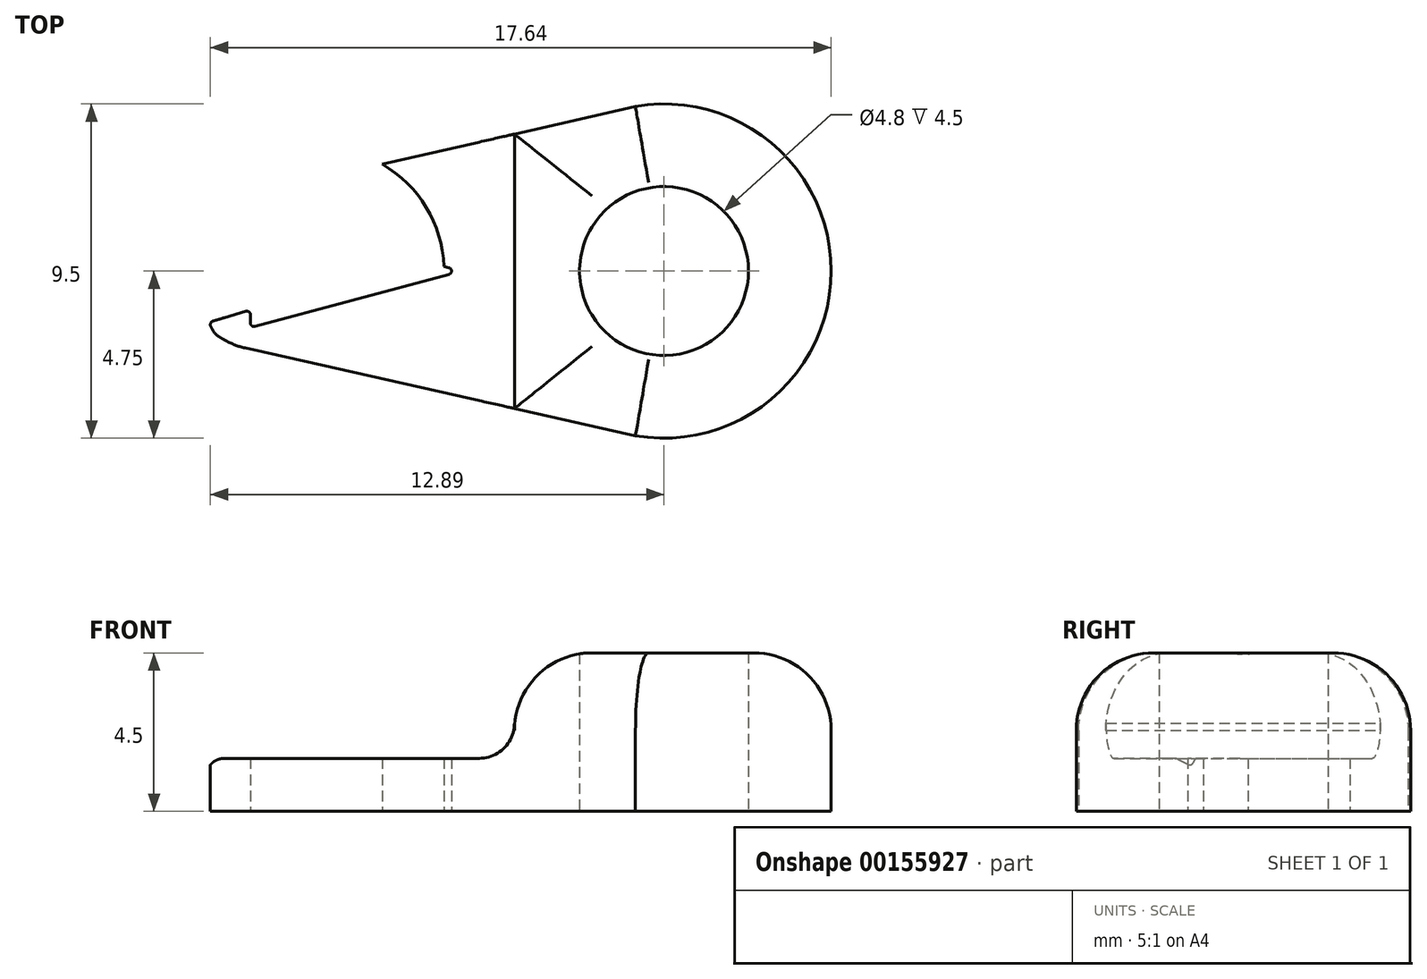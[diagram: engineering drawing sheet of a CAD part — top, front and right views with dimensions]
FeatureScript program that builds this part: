
annotation { "Feature Type Name" : "Feature", "Feature Type Description" : "" }
export const myFeature = defineFeature(function(context is Context, id is Id, definition is map)
    precondition{}
    {
        {
            var Q0;
            Q0=qCreatedBy(makeId("Top.planeOp"),FACE);
            var sketch = newSketch(context, id + "F0", { "sketchPlane" : qUnion([Q0])});
            skCircle(sketch, "E0", {"center": v(0, 0) * mm, "radius": 4.75 * mm});
            skCircle(sketch, "E1", {"center": v(0, 0) * mm, "radius": 2.4 * mm});
            skLineSegment(sketch, "E2", {"start": v(0, 0) * mm, "end": v(-5.75, 0) * mm});
            skArc(sketch, "E3", {"start": v(-12.88, -1.56) * mm, "mid": v(-12.85, -1.62) * mm, "end": v(-12.82, -1.68) * mm});
            skLineSegment(sketch, "E4", {"start": v(-6.11, 0.1) * mm, "end": v(-11.62, 1.57) * mm});
            skLineSegment(sketch, "E5", {"start": v(-6.11, -0.1) * mm, "end": v(-11.62, -1.57) * mm});
            skLineSegment(sketch, "E6", {"start": v(-11.75, 1.6) * mm, "end": v(-11.75, 1.1) * mm});
            skLineSegment(sketch, "E7", {"start": v(-11.75, 1.47) * mm, "end": v(-11.75, 1.23) * mm});
            skLineSegment(sketch, "E8", {"start": v(-11.87, 1.14) * mm, "end": v(-12.84, 1.37) * mm});
            skLineSegment(sketch, "E9", {"start": v(-11.75, -1.6) * mm, "end": v(-11.75, -1.1) * mm});
            skLineSegment(sketch, "E10", {"start": v(-11.88, -1.15) * mm, "end": v(-12.82, -1.42) * mm});
            skLineSegment(sketch, "E11.trimOffspring", {"start": v(-11.75, -1.24) * mm, "end": v(-11.75, -1.48) * mm});
            skArc(sketch, "E12.trimOffspring", {"start": v(-6.25, 0.13) * mm, "mid": v(-6.75, 1.81) * mm, "end": v(-8, 3.03) * mm});
            skPoint(sketch, "E13.endSnap0", {"position": v(-11.34, -2.73) * mm});
            skPoint(sketch, "E13.end.orphan", {"position": v(-12.93, -2.73) * mm});
            skLineSegment(sketch, "E14", {"start": v(-12.66, 1.82) * mm, "end": v(-12.5, 1.91) * mm});
            skLineSegment(sketch, "E15", {"start": v(-11.9, -2.19) * mm, "end": v(-0.8, -4.68) * mm});
            skLineSegment(sketch, "E16", {"start": v(-12.63, -1.88) * mm, "end": v(-12.45, -1.98) * mm});
            skArc(sketch, "E17.trimOffspring", {"start": v(-12.85, 1.62) * mm, "mid": v(-12.88, 1.57) * mm, "end": v(-12.9, 1.51) * mm});
            skLineSegment(sketch, "E18.trimOffspring", {"start": v(-0.94, 4.66) * mm, "end": v(-0.81, 4.68) * mm});
            skLineSegment(sketch, "E19.trimOffspring", {"start": v(-11.95, 2.13) * mm, "end": v(-0.81, 4.68) * mm});
            skPoint(sketch, "E20.orphan", {"position": v(-12.96, 1.9) * mm});
            skArc(sketch, "E21.trimOffspring", {"start": v(-8.04, -3.05) * mm, "mid": v(-6.77, -1.83) * mm, "end": v(-6.25, -0.13) * mm});
            skPoint(sketch, "E22.orphan", {"position": v(-9.75, -3.5) * mm});
            skPoint(sketch, "E23.orphan", {"position": v(-12.93, -1.96) * mm});
            skPoint(sketch, "E24.end.orphan", {"position": v(-12.93, -1.7) * mm});
            skPoint(sketch, "E25.end.orphan", {"position": v(-12.96, 1.65) * mm});
            skPoint(sketch, "E26.visualSharp", {"position": v(-11.75, 1.6) * mm});
            skArc(sketch, "E26.filletArc", {"start": v(-11.62, 1.57) * mm, "mid": v(-11.7, 1.55) * mm, "end": v(-11.75, 1.47) * mm});
            skPoint(sketch, "E27.visualSharp", {"position": v(-5.75, 0) * mm});
            skArc(sketch, "E27.filletArc", {"start": v(-6.11, -0.1) * mm, "mid": v(-6.04, 0) * mm, "end": v(-6.11, 0.1) * mm});
            skPoint(sketch, "E28.visualSharp", {"position": v(-11.75, -1.6) * mm});
            skArc(sketch, "E28.filletArc", {"start": v(-11.75, -1.48) * mm, "mid": v(-11.71, -1.56) * mm, "end": v(-11.62, -1.57) * mm});
            skPoint(sketch, "E29.visualSharp", {"position": v(-11.75, -1.1) * mm});
            skArc(sketch, "E29.filletArc", {"start": v(-11.75, -1.24) * mm, "mid": v(-11.8, -1.16) * mm, "end": v(-11.88, -1.15) * mm});
            skPoint(sketch, "E30.visualSharp", {"position": v(-11.75, 1.1) * mm});
            skArc(sketch, "E30.filletArc", {"start": v(-11.87, 1.14) * mm, "mid": v(-11.79, 1.16) * mm, "end": v(-11.75, 1.23) * mm});
            skPoint(sketch, "E31.visualSharp", {"position": v(-12.93, -1.46) * mm});
            skArc(sketch, "E31.filletArc", {"start": v(-12.82, -1.42) * mm, "mid": v(-12.88, -1.48) * mm, "end": v(-12.88, -1.56) * mm});
            skPoint(sketch, "E32.visualSharp", {"position": v(-12.96, 1.4) * mm});
            skArc(sketch, "E32.filletArc", {"start": v(-12.9, 1.51) * mm, "mid": v(-12.9, 1.43) * mm, "end": v(-12.84, 1.37) * mm});
            skPoint(sketch, "E33.visualSharp", {"position": v(-12.78, 1.75) * mm});
            skArc(sketch, "E33.filletArc", {"start": v(-12.66, 1.82) * mm, "mid": v(-12.77, 1.74) * mm, "end": v(-12.85, 1.62) * mm});
            skPoint(sketch, "E34.visualSharp", {"position": v(-12.24, 2.06) * mm});
            skArc(sketch, "E34.filletArc", {"start": v(-11.95, 2.13) * mm, "mid": v(-12.23, 2.04) * mm, "end": v(-12.5, 1.91) * mm});
            skPoint(sketch, "E35.visualSharp", {"position": v(-12.2, -2.12) * mm});
            skArc(sketch, "E35.filletArc", {"start": v(-12.45, -1.98) * mm, "mid": v(-12.19, -2.1) * mm, "end": v(-11.9, -2.19) * mm});
            skPoint(sketch, "E36.visualSharp", {"position": v(-12.74, -1.81) * mm});
            skArc(sketch, "E36.filletArc", {"start": v(-12.82, -1.68) * mm, "mid": v(-12.74, -1.8) * mm, "end": v(-12.63, -1.88) * mm});
            skLineSegment(sketch, "E37", {"start": v(-12.96, 1.8) * mm, "end": v(-12.93, -2.85) * mm});
            skSolve(sketch);
        }
        {
            var Q0;
            Q0=qCreatedBy(makeId("Front.planeOp"),FACE);
            var sketch = newSketch(context, id + "F1", { "sketchPlane" : qUnion([Q0])});
            skLineSegment(sketch, "E38", {"start": v(0, 0) * mm, "end": v(-13, 0) * mm});
            skLineSegment(sketch, "E39", {"start": v(-13, 0) * mm, "end": v(-13, 1) * mm});
            skLineSegment(sketch, "E40", {"start": v(-12.5, 1.5) * mm, "end": v(-8, 1.5) * mm});
            skLineSegment(sketch, "E41", {"start": v(-8, 1.5) * mm, "end": v(-5.25, 1.5) * mm});
            skLineSegment(sketch, "E42", {"start": v(-4.25, 2.3) * mm, "end": v(-4.25, 2.5) * mm});
            skLineSegment(sketch, "E43", {"start": v(-2.05, 4.5) * mm, "end": v(0, 4.5) * mm});
            skLineSegment(sketch, "E44", {"start": v(0, 4.5) * mm, "end": v(0, 0) * mm});
            skPoint(sketch, "E45.visualSharp", {"position": v(-4.25, 4.5) * mm});
            skArc(sketch, "E45.filletArc", {"start": v(-2.05, 4.5) * mm, "mid": v(-3.6, 3.86) * mm, "end": v(-4.25, 2.3) * mm});
            skPoint(sketch, "E46.visualSharp", {"position": v(-13, 1.5) * mm});
            skArc(sketch, "E46.filletArc", {"start": v(-12.5, 1.5) * mm, "mid": v(-12.85, 1.35) * mm, "end": v(-13, 1) * mm});
            skPoint(sketch, "E47.visualSharp", {"position": v(-4.25, 1.5) * mm});
            skArc(sketch, "E47.filletArc", {"start": v(-5.25, 1.5) * mm, "mid": v(-4.54, 1.8) * mm, "end": v(-4.25, 2.5) * mm});
            skLineSegment(sketch, "E48", {"start": v(0, 4.5) * mm, "end": v(0, 5.81) * mm});
            skLineSegment(sketch, "E49", {"start": v(0, 5.81) * mm, "end": v(-16.42, 5.81) * mm});
            skLineSegment(sketch, "E50", {"start": v(-16.42, 5.81) * mm, "end": v(-16.42, 0) * mm});
            skLineSegment(sketch, "E51", {"start": v(-16.42, 0) * mm, "end": v(-13, 0) * mm});
            skSolve(sketch);
        }
        {
            var Q0;
            Q0=makeQuery(id+"F0.imprint","IMPRINT",FACE,{"disambiguationData":[TD([[makeQuery(id+"F0.imprint","IMPRINT",EDGE,{"derivedFrom":sQuery(id+"F0.wireOp",EDGE,"E1")}),-1.0]])]});
            extrude(context, id + "F2", {"entities" : qUnion([Q0]), "depth" : 4.5 * mm});
        }
        {
            var Q0;
            {var subQ3=sQuery(id+"F0.wireOp",EDGE,"E21.trimOffspring");Q0=makeQuery(id+"F0.imprint","IMPRINT",FACE,{"disambiguationData":[TD([[makeQuery(id+"F0.imprint","IMPRINT",EDGE,{"derivedFrom":subQ3}),-1.0]])]});}
            var Q1;
            {var subQ3=sQuery(id+"F0.wireOp",EDGE,"E12.trimOffspring");Q1=makeQuery(id+"F0.imprint","IMPRINT",FACE,{"disambiguationData":[TD([[makeQuery(id+"F0.imprint","IMPRINT",EDGE,{"derivedFrom":subQ3}),-1.0]])]});}
            extrude(context, id + "F3", {"entities" : qUnion([Q0, Q1]), "operationType" : NewBodyOperationType.ADD, "depth" : 4 * mm});
        }
        {
            var Q0;
            Q0=makeQuery(id+"F0.imprint","IMPRINT",FACE,{"disambiguationData":[TD([[makeQuery(id+"F0.imprint","IMPRINT",EDGE,{"derivedFrom":sQuery(id+"F0.wireOp",EDGE,"E3")}),1.0]])]});
            var Q1;
            {var subQ1=sQuery(id+"F0.wireOp",EDGE,"E7");Q1=makeQuery(id+"F0.imprint","IMPRINT",FACE,{"disambiguationData":[TD([[makeQuery(id+"F0.imprint","IMPRINT",EDGE,{"derivedFrom":subQ1}),-1.0]])]});}
            extrude(context, id + "F4", {"entities" : qUnion([Q0, Q1]), "operationType" : NewBodyOperationType.ADD, "depth" : 4 * mm});
        }
        {
            var Q0;
            Q0=makeQuery(id+"F1.imprint","IMPRINT",FACE,{"disambiguationData":[TD([[makeQuery(id+"F1.imprint","IMPRINT",EDGE,{"derivedFrom":sQuery(id+"F1.wireOp",EDGE,"E39")}),1.0]])]});
            extrude(context, id + "F5", {"entities" : qUnion([Q0]), "operationType" : NewBodyOperationType.REMOVE, "depth" : 5 * mm, "hasSecondDirection" : true, "secondDirectionOppositeDirection" : true, "secondDirectionDepth" : 5 * mm});
        }
        {
            var Q0;
            {var subQ0=sQuery(id+"F0.wireOp",EDGE,"E0");Q0=makeQuery(id+"F2.opExtrude","CAP_EDGE",EDGE,{"disambiguationData":[OSD([subQ0]),TDD([makeQuery(id+"F0.imprint","IMPRINT",EDGE,{"disambiguationData":[TD([[makeQuery(id+"F0.imprint","INTERSECT",VERTEX,{"disambiguationData":[OD(0.0)],"derivedFrom":[subQ0,sQuery(id+"F0.wireOp",EDGE,"E15")]}),-1.0]])],"derivedFrom":subQ0})])],"isStart":false});}
            fillet(context, id + "F6", {"entities" : qUnion([Q0]), "radius" : 2.2 * mm, "allowEdgeOverflow" : false});
        }
    });
